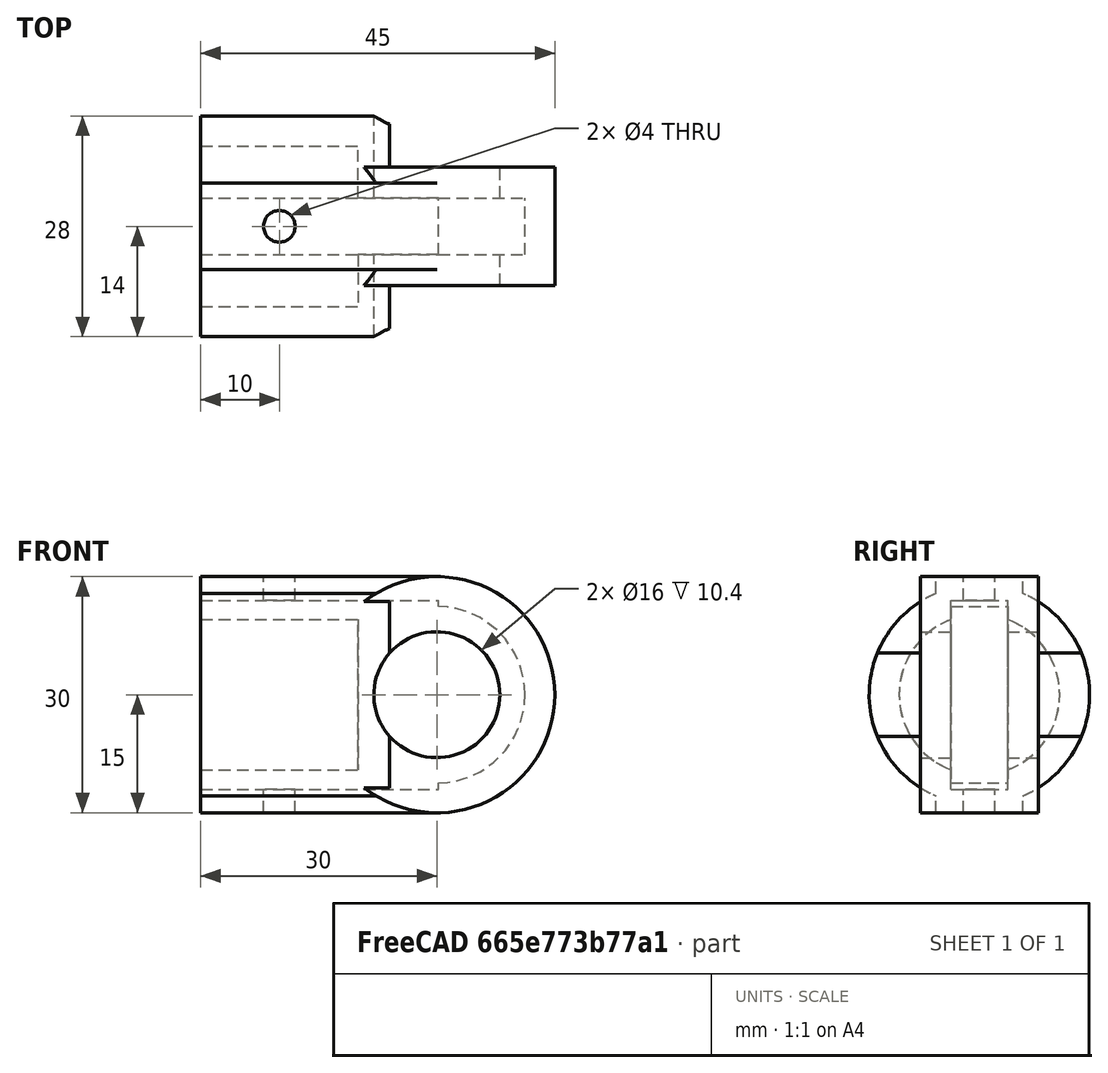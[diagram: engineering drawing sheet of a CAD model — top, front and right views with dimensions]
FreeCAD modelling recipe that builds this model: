
FCSTD DOCUMENT  (FreeCAD 0.17R13522 (Git))
Label: connector-bearing
License: All rights reserved
LicenseURL: http://en.wikipedia.org/wiki/All_rights_reserved
objects: Part::Cylinder×6, Part::Box×2, Part::MultiFuse×2, Part::Cut×1
note: 11 computed .brp shape members not serialized (recipe doc carries the construction recipe); baked Part::Feature solids carry a one-line shape summary decoded from their .brp

FEATURE [Part::Cylinder] Cylinder  label="Bearing"
  Angle = 360
  AttacherType = Attacher::AttachEngine3D
  Height = 7.2
  Placement = pos=(0,-3.6,0) rot=(-1,0,0;1.5708rad)
  Radius = 11.2
FEATURE [Part::Cylinder] Cylinder001
  Angle = 360
  AttacherType = Attacher::AttachEngine3D
  Height = 15
  Placement = pos=(0,-7.5,0) rot=(-1,0,0;1.5708rad)
  Radius = 15
FEATURE [Part::Cylinder] Cylinder002
  Angle = 360
  AttacherType = Attacher::AttachEngine3D
  Height = 24
  Placement = pos=(-30,0,0) rot=(0,1,0;1.5708rad)
  Radius = 14
FEATURE [Part::Cylinder] Cylinder003  label="Pipe"
  Angle = 360
  AttacherType = Attacher::AttachEngine3D
  Height = 20
  Placement = pos=(-30,0,0) rot=(0,1,0;1.5708rad)
  Radius = 10.2
FEATURE [Part::Cylinder] Cylinder004  label="Cylinder"
  Angle = 360
  AttacherType = Attacher::AttachEngine3D
  Height = 30
  Placement = pos=(0,-15,0) rot=(-1,0,0;1.5708rad)
  Radius = 8
FEATURE [Part::Box] Box001  label="Cube001"
  AttacherType = Attacher::AttachEngine3D
  Height = 30
  Length = 30
  Placement = pos=(-30,-5.5,-15) rot=(0,0,1;0rad)
  Width = 11
FEATURE [Part::MultiFuse] Fusion  label="Positive Fusion"
  Shapes = -> [Cylinder001,Cylinder002,Box001]
FEATURE [Part::Cylinder] Cylinder005  label="Cylinder003"
  Angle = 360
  AttacherType = Attacher::AttachEngine3D
  Height = 30
  Placement = pos=(-20,0,-15) rot=(0,0,1;0rad)
  Radius = 2
FEATURE [Part::Box] Box  label="Cube"
  AttacherType = Attacher::AttachEngine3D
  Height = 24
  Length = 30.2
  Placement = pos=(-30,-3.6,-12) rot=(0,0,1;0rad)
  Width = 7.2
FEATURE [Part::MultiFuse] Fusion001  label="Negative Fusion"
  Shapes = -> [Cylinder004,Cylinder003,Cylinder,Cylinder005,Box]
FEATURE [Part::Cut] Cut
  Base = -> Fusion
  Tool = -> Fusion001
